# Revit family: Cabinet_Base_Doors
name_source: partatom
category: Casework
units: mm (PartAtom-declared; Revit-internal decimal feet)

## family parameters
Always vertical = Yes
Classification Number = 23.40.35.11.11
Cut with Voids When Loaded = No
Room Calculation Point = No
Shared = No
Work Plane-Based = No

## types (1)
- ByType
    Assembly Code = C1030410
    Building Codes = http://www.iccsafe.org
    Construction Details = http://www.arcat.com
    Default Elevation = 0' - 0"
    Depth = 2' - 0"
    Description = 36" 1 Drawer - 2 Door Base Cabinet
    Door Finish = <By Category>
    Door Frame Material = ARCAT - Wood - Cherry_Domestic
    Door Panel Material = ARCAT - Wood - Cherry_Domestic
    Door Style = Drawer - Shaker : Door
    Door Thickness = 0' - 0 3/4"
    DoorCount = 2
    Drawer Count = 2
    Drawer Height = 0' - 5"
    Drawer Style = Drawer - Shaker : Drawer
    Drawer Type = Full Extension
    Expected Lifespan (Years) = 20
    Frame Finish = ARCAT - Wood - Maple_Hard
    FrameReveal = 0' - 0 1/4"
    Glass Type = <By Category>
    Glide Type = Side and Center Roller Bearing
    Green Building-LEED = http://www.arcat.com
    Hardware Type = Recessed Cup Self Closing Hinges
    Height = 2' - 6"
    Installation Phase = Finish Carpentry
    Installation_Fabricaton = http://www.nkba.org
    Keynote = 12350
    Left Side Panel Finish = ARCAT - Wood - Maple_Hard
    Maintainence Schedule (Months) = 1
    Manufacturer = Generic
    Manufacturer Fax = (203) 939-2444
    Manufacturer Website = http://www.arcat.com
    Model = Generic Base Cabinet
    Panel Thickness = 0' - 0 3/4"
    Product Data = http://www.arcat.com
    Product Properties = http://www.arcat.com
    Right Side Panel Finish = ARCAT - Wood - Maple_Hard
    Specification = http://www.arcat.com
    Toe Kick Depth = 0' - 2"
    Toe Kick Height = 0' - 4"
    Warranty Duration (Years) = 5
    Width = 2' - 0"

## geometry (parser evidence)
native form markers: Blend x3, Sweep x10
no freeform markers — native parametric forms only
